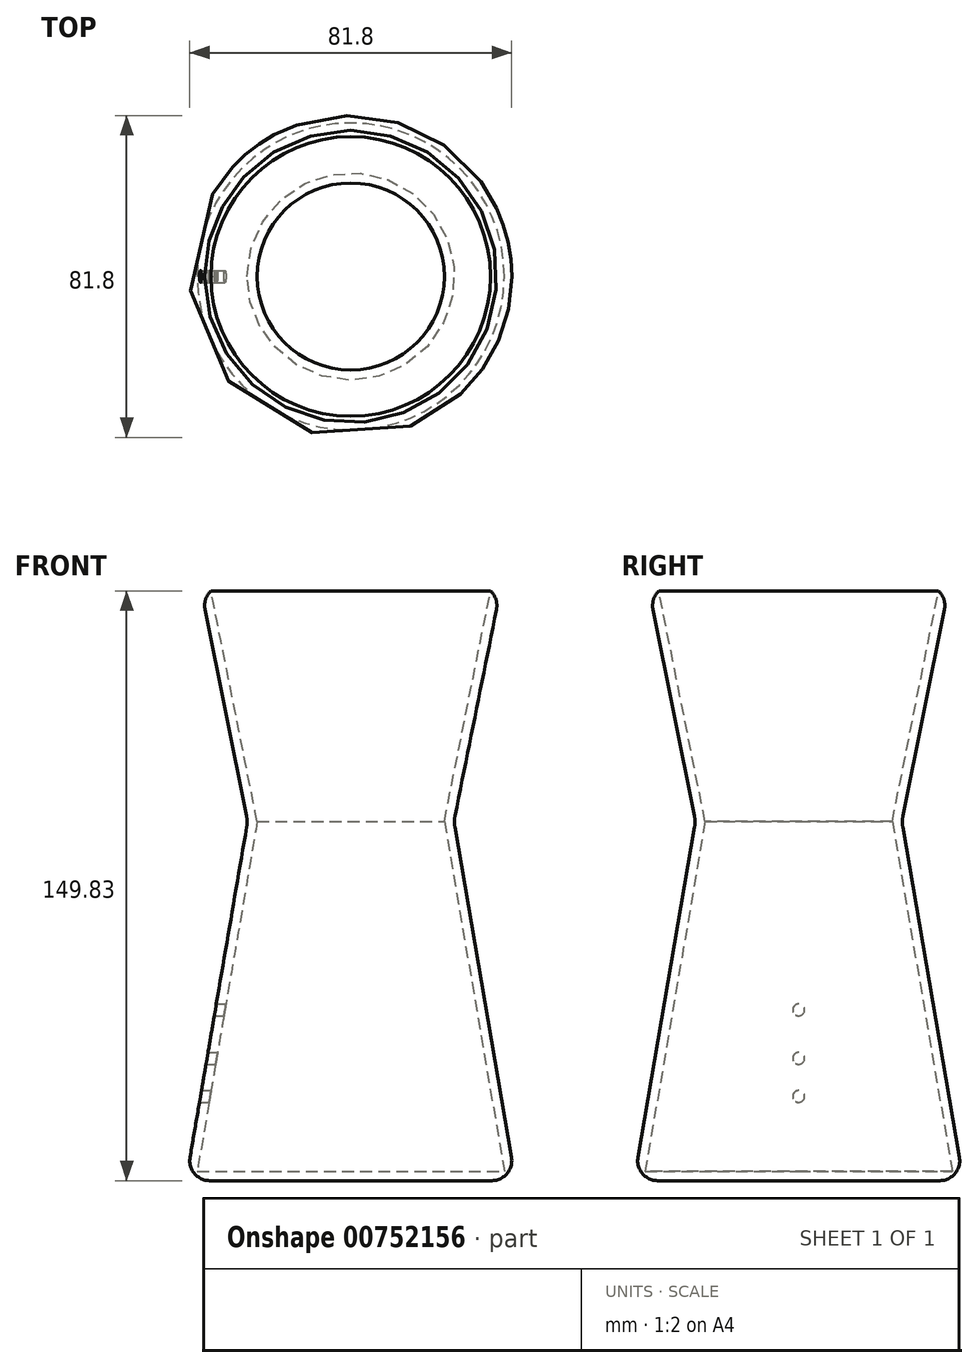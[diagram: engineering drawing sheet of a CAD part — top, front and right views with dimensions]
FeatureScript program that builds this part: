
annotation { "Feature Type Name" : "Feature", "Feature Type Description" : "" }
export const myFeature = defineFeature(function(context is Context, id is Id, definition is map)
    precondition{}
    {
        {
            var Q0;
            Q0=qCreatedBy(makeId("Front.planeOp"),FACE);
            var sketch = newSketch(context, id + "F0", { "sketchPlane" : qUnion([Q0])});
            skLineSegment(sketch, "E0", {"start": v(0, 75.41) * mm, "end": v(-37.96, 75.41) * mm});
            skLineSegment(sketch, "E1", {"start": v(-37.96, 75.41) * mm, "end": v(-26.2, 16.81) * mm});
            skLineSegment(sketch, "E2", {"start": v(-26.2, 16.81) * mm, "end": v(-41.85, -74.42) * mm});
            skLineSegment(sketch, "E3", {"start": v(-41.85, -74.42) * mm, "end": v(0, -74.42) * mm});
            skLineSegment(sketch, "E4", {"start": v(0, -74.42) * mm, "end": v(0, 75.41) * mm});
            skLineSegment(sketch, "E5.0", {"start": v(-23.76, 16.85) * mm, "end": v(-39, -72.02) * mm});
            skLineSegment(sketch, "E5.1", {"start": v(-35.6, 75.89) * mm, "end": v(-23.76, 16.85) * mm});
            skLineSegment(sketch, "E6.0", {"start": v(-41.85, -72.02) * mm, "end": v(-41.44, -72.02) * mm});
            skLineSegment(sketch, "E7.trimOffspring", {"start": v(-39, -72.02) * mm, "end": v(0, -72.02) * mm});
            skLineSegment(sketch, "E8.trimOffspring", {"start": v(-39.41, -74.42) * mm, "end": v(-39.48, -74.82) * mm});
            skSolve(sketch);
        }
        {
            var Q0;
            {var subQ4=sQuery(id+"F0.wireOp",EDGE,"E1");Q0=makeQuery(id+"F0.imprint","IMPRINT",FACE,{"disambiguationData":[TD([[makeQuery(id+"F0.imprint","IMPRINT",EDGE,{"derivedFrom":subQ4}),1.0]])]});}
            var Q1;
            Q1=sQuery(id+"F0.wireOp",EDGE,"E4");
            revolve(context, id + "F1", {"surfaceOperationType" : NewSurfaceOperationType.NEW, "entities" : qUnion([Q0]), "axis" : qUnion([Q1]), "revolveType" : RevolveType.FULL});
        }
        {
            var Q0;
            Q0=makeQuery(id+"F1.opRevolve","SWEPT_EDGE",EDGE,{"disambiguationData":[OSD([sQuery(id+"F0.wireOp",EDGE,"E0"),sQuery(id+"F0.wireOp",EDGE,"E1")])]});
            var Q1;
            Q1=makeQuery(id+"F1.opRevolve","SWEPT_EDGE",EDGE,{"disambiguationData":[OSD([sQuery(id+"F0.wireOp",EDGE,"E2"),sQuery(id+"F0.wireOp",EDGE,"E3")])]});
            fillet(context, id + "F2", {"entities" : qUnion([Q0, Q1]), "radius" : 5.08 * mm, "tangentPropagation" : true, "allowEdgeOverflow" : false});
        }
        {
            var Q0;
            Q0=makeQuery(id+"F1.opRevolve","SWEPT_EDGE",EDGE,{"disambiguationData":[OSD([sQuery(id+"F0.wireOp",EDGE,"E1"),sQuery(id+"F0.wireOp",EDGE,"E2")])]});
            fillet(context, id + "F3", {"entities" : qUnion([Q0]), "radius" : 7.62 * mm, "tangentPropagation" : true, "allowEdgeOverflow" : false});
        }
        {
            var Q0;
            Q0=qCreatedBy(makeId("Right.planeOp"),FACE);
            var sketch = newSketch(context, id + "F4", { "sketchPlane" : qUnion([Q0])});
            skCircle(sketch, "E9", {"center": v(0, -31.03) * mm, "radius": 1.5 * mm});
            skCircle(sketch, "E10", {"center": v(0, -43.35) * mm, "radius": 1.5 * mm});
            skCircle(sketch, "E11", {"center": v(0, -53.02) * mm, "radius": 1.5 * mm});
            skSolve(sketch);
        }
        {
            var Q0;
            Q0 = qSketchRegion(id + "F4", true);
            extrude(context, id + "F5", {"entities" : qUnion([Q0]), "operationType" : NewBodyOperationType.REMOVE, "endBound" : BoundingType.THROUGH_ALL, "oppositeDirection" : true, "depth" : 25 * mm, "offsetDistance" : 25 * mm});
        }
    });
